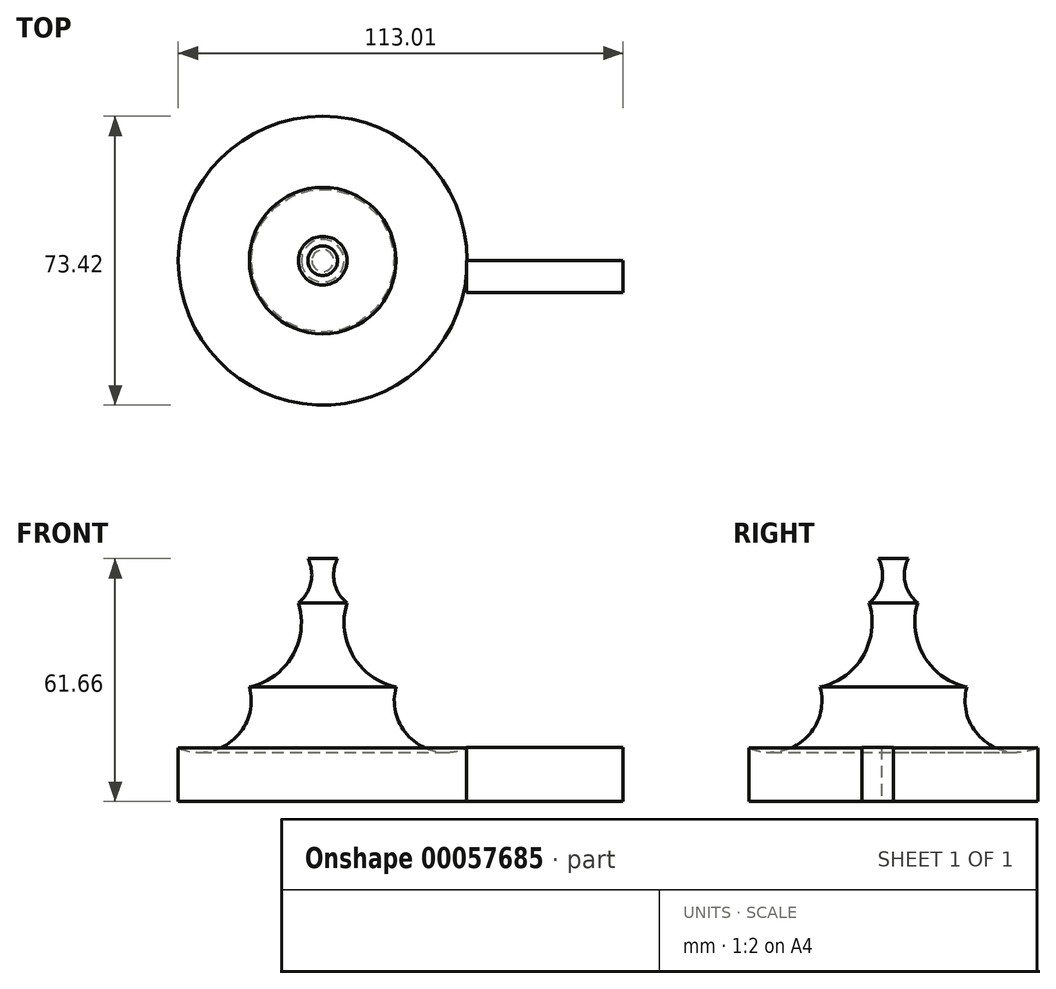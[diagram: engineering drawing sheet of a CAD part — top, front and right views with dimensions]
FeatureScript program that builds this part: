
annotation { "Feature Type Name" : "Feature", "Feature Type Description" : "" }
export const myFeature = defineFeature(function(context is Context, id is Id, definition is map)
    precondition{}
    {
        {
            var Q0;
            Q0=qCreatedBy(makeId("Front.planeOp"),FACE);
            var sketch = newSketch(context, id + "F0", { "sketchPlane" : qUnion([Q0])});
            skLineSegment(sketch, "E0.bottom", {"start": v(0, 0) * mm, "end": v(36.7, 0) * mm});
            skLineSegment(sketch, "E0.top", {"start": v(0, 61.66) * mm, "end": v(3.77, 61.66) * mm});
            skLineSegment(sketch, "E0.left", {"start": v(0, 0) * mm, "end": v(0, 61.66) * mm});
            skLineSegment(sketch, "E0.right", {"start": v(36.7, 0) * mm, "end": v(36.7, 13.62) * mm});
            skArc(sketch, "E1", {"start": v(3.77, 61.66) * mm, "mid": v(2.96, 55.6) * mm, "end": v(6.18, 50.42) * mm});
            skArc(sketch, "E2", {"start": v(6.18, 50.42) * mm, "mid": v(7.7, 36.98) * mm, "end": v(18.63, 29.01) * mm});
            skArc(sketch, "E3", {"start": v(18.63, 29.01) * mm, "mid": v(22.8, 15.59) * mm, "end": v(36.7, 13.62) * mm});
            skArc(sketch, "E4.trimOffspring", {"start": v(36.7, 36.83) * mm, "mid": v(36.87, 37.11) * mm, "end": v(37.02, 37.4) * mm});
            skLineSegment(sketch, "E5.trimOffspring", {"start": v(36.7, 36.83) * mm, "end": v(36.7, 37.54) * mm});
            skArc(sketch, "E6.trimOffspring", {"start": v(37.02, 37.4) * mm, "mid": v(36.86, 37.47) * mm, "end": v(36.7, 37.54) * mm});
            skSolve(sketch);
        }
        {
            var Q0;
            Q0=makeQuery(id+"F0.imprint","IMPRINT",FACE,{"disambiguationData":[TD([[makeQuery(id+"F0.imprint","IMPRINT",EDGE,{"derivedFrom":sQuery(id+"F0.wireOp",EDGE,"E0.bottom")}),1.0]])]});
            var Q1;
            Q1=sQuery(id+"F0.wireOp",EDGE,"E0.left");
            var Q2;
            Q2=sQuery(id+"F0.wireOp",EDGE,"E0.top");
            var Q3;
            Q3=sQuery(id+"F0.wireOp",EDGE,"E1");
            var Q4;
            Q4=sQuery(id+"F0.wireOp",EDGE,"E2");
            var Q5;
            Q5=sQuery(id+"F0.wireOp",EDGE,"E3");
            var Q6;
            Q6=sQuery(id+"F0.wireOp",EDGE,"E0.right");
            var Q7;
            Q7=sQuery(id+"F0.wireOp",EDGE,"E0.bottom");
            var Q8;
            Q8=sQuery(id+"F0.wireOp",EDGE,"E0.left");
            revolve(context, id + "F1", {"entities" : qUnion([Q0]), "surfaceEntities" : qUnion([Q1, Q2, Q3, Q4, Q5, Q6, Q7]), "axis" : qUnion([Q8]), "revolveType" : RevolveType.FULL});
        }
        {
            var Q0;
            Q0=qCreatedBy(makeId("Front.planeOp"),FACE);
            var sketch = newSketch(context, id + "F2", { "sketchPlane" : qUnion([Q0])});
            skLineSegment(sketch, "E7.bottom", {"start": v(36.58, 13.76) * mm, "end": v(76.3, 13.76) * mm});
            skLineSegment(sketch, "E7.top", {"start": v(36.58, 0) * mm, "end": v(76.3, 0) * mm});
            skLineSegment(sketch, "E7.left", {"start": v(36.58, 13.76) * mm, "end": v(36.58, 0) * mm});
            skLineSegment(sketch, "E7.right", {"start": v(76.3, 13.76) * mm, "end": v(76.3, 0) * mm});
            skSolve(sketch);
        }
        {
            var Q0;
            Q0 = qSketchRegion(id + "F2", true);
            extrude(context, id + "F3", {"entities" : qUnion([Q0]), "operationType" : NewBodyOperationType.ADD, "depth" : 8.05 * mm});
        }
    });
